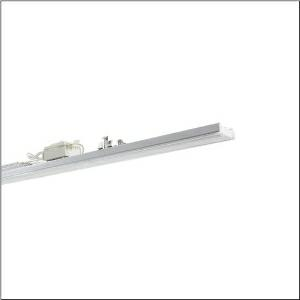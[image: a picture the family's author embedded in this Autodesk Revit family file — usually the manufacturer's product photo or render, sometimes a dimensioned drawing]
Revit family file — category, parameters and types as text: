
# Revit family: licross_r__11_recessed_mo_51tl11mn4axg_a2d7
name_source: partatom
category: Lighting Fixtures
units: mm (PartAtom-declared; Revit-internal decimal feet)

## family parameters
Cut with Voids When Loaded = No
Host = Face
Light Source = No
Part Type = Normal
Room Calculation Point = No
Round Connector Dimension = Use Diameter
Shared = No

## types (1)
- --- (1 x LED, 10130 lm, 55.2 W, 4000K)
    Apparent Load = 55 VA
    CIE Flux Codes = 89 96 99 100 100
    Color Rendering = 80
    Color Temperature = 4000K
    Default Elevation = 1800 mm
    Description = Licross® 11 Recessed MO, luminaire insert, of sheet steel, coil coated, white, length: 1.500mm, width: 66mm, height: 67mm, LED rated luminous flux: 10.130lm, light colour: 840, control gear: ON/OFF Multilumen, with plug, 3-pole, with phase selection, mains connection: 220..240V, AC, 50/60Hz, rated input power: 55W, halogen-free wiring, primary light control with lens, of plastic, primary optical cover: cover, of PMMA, light emission: direct distribution, primary light characteristic: symmetric, protection rating (complete): IP40, insulation class (complete): insulation class I (protective earthing), certification: CE, ENEC, VDE, UKCA, protection symbol: D if used in an environment without relevant dust loads with corresponding accessories, impact resistance: IK06, permissible ambient temperature for indoor applications: -35..+40°C, corresponds to IFS (International Featured Standards) requirements for safety and quality in the food industry, reducing of maximum allowable ambient temperature of 5°C with ceiling mounting, packaging unit: 1 piece
    Height = 58 mm
    Lamp = 1 x LED
    Lamp Light Flux = 10130 lm
    Lamp Power = 55.2 W
    Lamp count = 1
    Length = 1500 mm
    Luminous efficacy = 184 lm/W
    Manufacturer = Siteco
    ModVariant = No
    Model = 51TL11MN4AXG
    Mounting Place = Ceiling
    Mounting Type = Pendant
    Number of Poles = 1
    OnlyDefault = Yes
    Power Factor = 1
    Product Name = Licross® 11 Recessed MO
    Product group = luminaire insert
    ProductGroupID = 902
    Protection Class = Protection class I
    Protection Degree = IP 40
    RLX_Detail_Level = 1
    RLX_Emergency_Light_Flux = 0 lm
    RLX_Emergency_Type = 0
    RLX_Emergency_Type_DB = No
    RlxData = <blob elided: 22153 chars, md5=bc4e5b6a>
    Socket = socket
    Standby Power = 0 W
    System Light Flux = 10130 lm
    System Power = 55 W
    Type Comments = factory setting: luminous flux: 100 % | (A | C | E) | 126 mA
    Type Image = l_1296930.jpg
    URL = http://relux.com
    VarID = @adj_084502
    Voltage = 0 V
    Weight = 0.00 kg
    Width = 66 mm

## geometry (parser evidence)
native form markers: Blend x4, Sweep x10
no freeform markers — native parametric forms only
